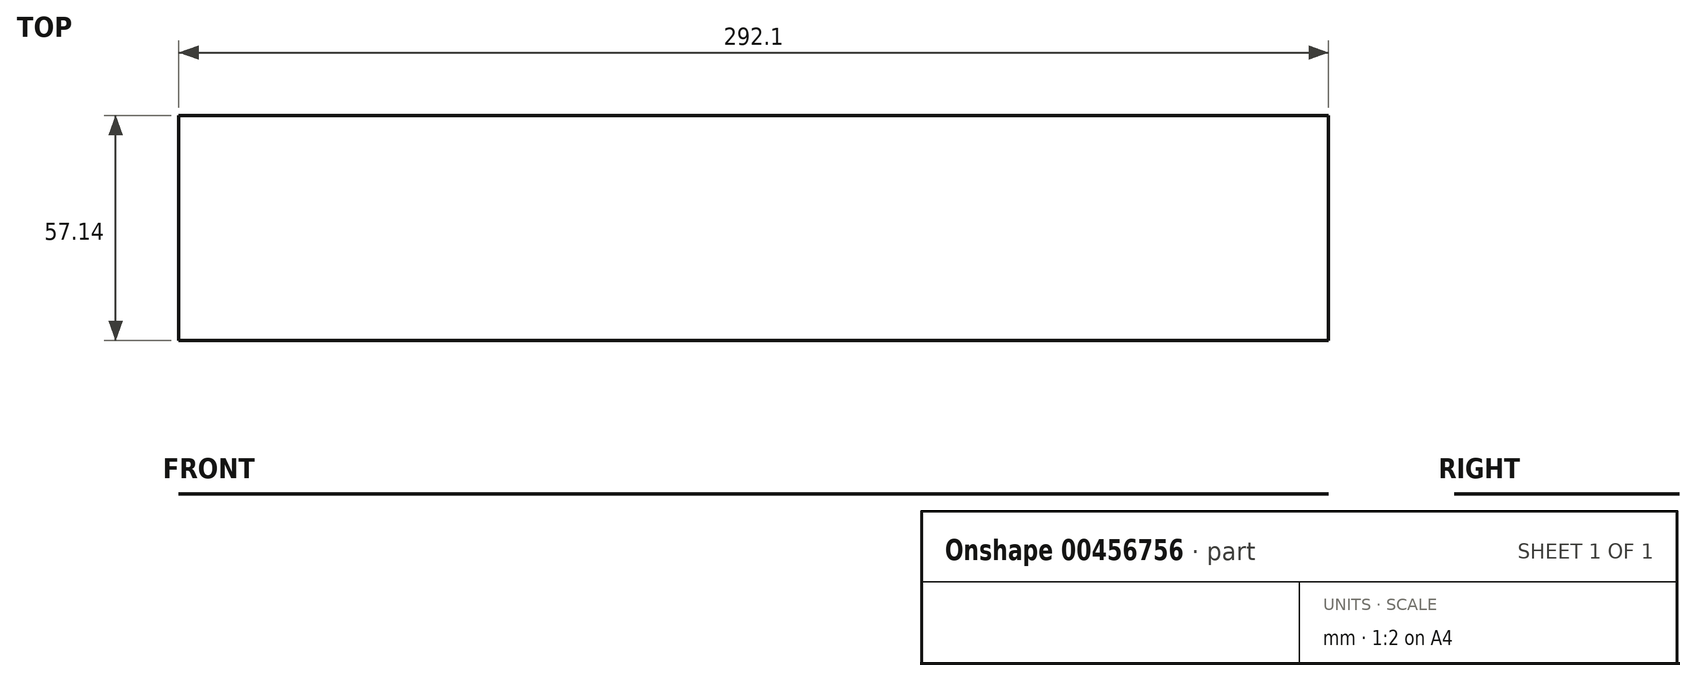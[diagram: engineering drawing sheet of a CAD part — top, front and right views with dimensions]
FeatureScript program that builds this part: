
annotation { "Feature Type Name" : "Feature", "Feature Type Description" : "" }
export const myFeature = defineFeature(function(context is Context, id is Id, definition is map)
    precondition{}
    {
        {
            var Q0;
            Q0=qCreatedBy(makeId("Top.planeOp"),FACE);
            var sketch = newSketch(context, id + "F0", { "sketchPlane" : qUnion([Q0])});
            skLineSegment(sketch, "E0.bottom", {"start": v(-146.05, 28.58) * mm, "end": v(146.05, 28.58) * mm});
            skLineSegment(sketch, "E0.top", {"start": v(-146.05, -28.58) * mm, "end": v(146.05, -28.58) * mm});
            skLineSegment(sketch, "E0.left", {"start": v(-146.05, 28.58) * mm, "end": v(-146.05, -28.57) * mm});
            skLineSegment(sketch, "E0.right", {"start": v(146.05, 28.57) * mm, "end": v(146.05, -28.57) * mm});
            skPoint(sketch, "E0.middle", {"position": v(0, 0) * mm});
            skSolve(sketch);
        }
        {
            var Q0;
            Q0=makeQuery(id+"F0.imprint","IMPRINT",FACE,{"disambiguationData":[TD([[makeQuery(id+"F0.imprint","IMPRINT",EDGE,{"derivedFrom":sQuery(id+"F0.wireOp",EDGE,"E0.bottom")}),-1.0]])]});
            extrude(context, id + "F1", {"entities" : qUnion([Q0]), "depth" : 1 / 203.2 * mm});
        }
    });
